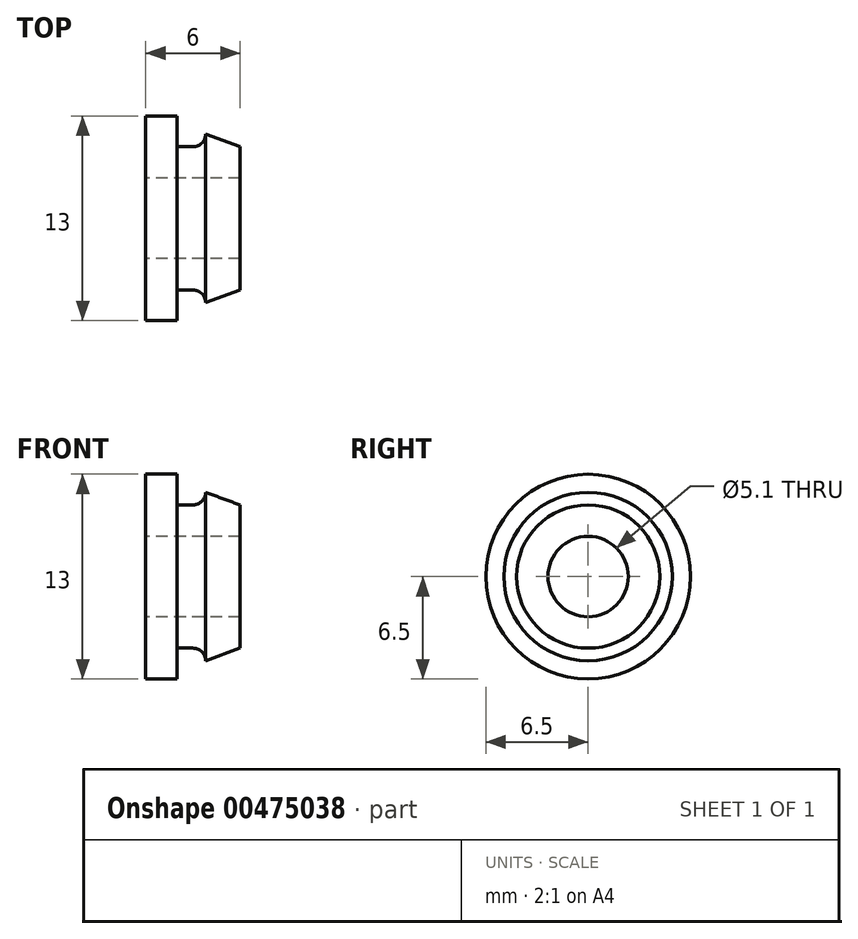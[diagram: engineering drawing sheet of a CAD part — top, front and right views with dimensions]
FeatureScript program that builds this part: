
annotation { "Feature Type Name" : "Feature", "Feature Type Description" : "" }
export const myFeature = defineFeature(function(context is Context, id is Id, definition is map)
    precondition{}
    {
        {
            var Q0;
            Q0=qCreatedBy(makeId("Front.planeOp"),FACE);
            var sketch = newSketch(context, id + "F0", { "sketchPlane" : qUnion([Q0])});
            skLineSegment(sketch, "E0", {"start": v(0, 0) * mm, "end": v(6, 0) * mm, "construction": true});
            skLineSegment(sketch, "E1", {"start": v(6, 0) * mm, "end": v(6, 2.55) * mm, "construction": true});
            skLineSegment(sketch, "E2", {"start": v(6, 2.55) * mm, "end": v(0, 2.55) * mm});
            skLineSegment(sketch, "E3", {"start": v(0, 0) * mm, "end": v(0, 6.5) * mm});
            skLineSegment(sketch, "E4", {"start": v(0, 6.5) * mm, "end": v(2, 6.5) * mm});
            skLineSegment(sketch, "E5", {"start": v(2, 6.5) * mm, "end": v(2, 4.55) * mm});
            skLineSegment(sketch, "E6", {"start": v(6, 4.55) * mm, "end": v(6, 2.55) * mm});
            skLineSegment(sketch, "E7", {"start": v(2, 4.55) * mm, "end": v(3.8, 4.55) * mm});
            skLineSegment(sketch, "E8", {"start": v(3.8, 4.55) * mm, "end": v(3.8, 5.35) * mm});
            skLineSegment(sketch, "E9", {"start": v(3.8, 5.35) * mm, "end": v(6, 4.55) * mm});
            skSolve(sketch);
        }
        {
            var Q0;
            {var subQ2=sQuery(id+"F0.wireOp",EDGE,"E2");Q0=makeQuery(id+"F0.imprint","IMPRINT",FACE,{"disambiguationData":[TD([[makeQuery(id+"F0.imprint","IMPRINT",EDGE,{"derivedFrom":subQ2}),-1.0]])]});}
            var Q1;
            Q1=sQuery(id+"F0.wireOp",EDGE,"E0");
            revolve(context, id + "F1", {"entities" : qUnion([Q0]), "axis" : qUnion([Q1]), "revolveType" : RevolveType.FULL});
        }
        {
            var Q0;
            Q0=makeQuery(id+"F1.opRevolve","SWEPT_EDGE",EDGE,{"disambiguationData":[OSD([sQuery(id+"F0.wireOp",EDGE,"E7"),sQuery(id+"F0.wireOp",EDGE,"E8")])]});
            fillet(context, id + "F2", {"entities" : qUnion([Q0]), "radius" : 0.8 * mm, "tangentPropagation" : true, "allowEdgeOverflow" : false});
        }
    });
